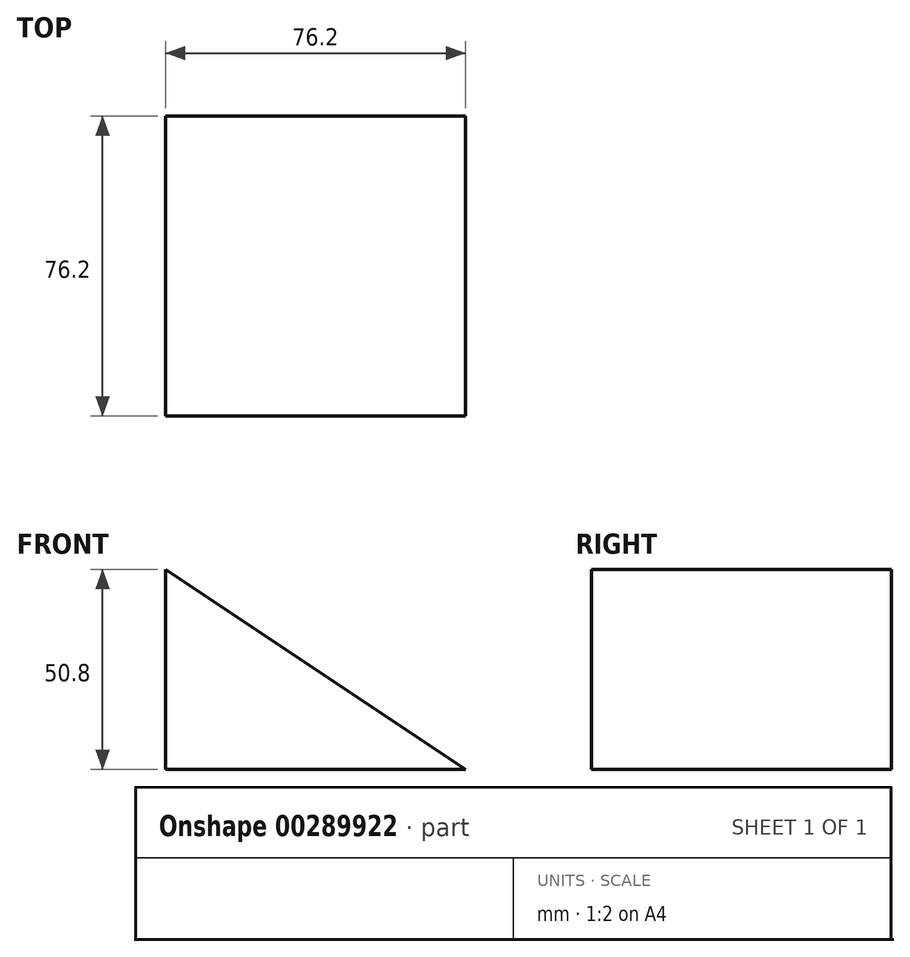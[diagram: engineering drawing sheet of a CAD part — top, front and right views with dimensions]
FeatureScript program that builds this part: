
annotation { "Feature Type Name" : "Feature", "Feature Type Description" : "" }
export const myFeature = defineFeature(function(context is Context, id is Id, definition is map)
    precondition{}
    {
        {
            var Q0;
            Q0=qCreatedBy(makeId("Front.planeOp"),FACE);
            var sketch = newSketch(context, id + "F0", { "sketchPlane" : qUnion([Q0])});
            skLineSegment(sketch, "E0", {"start": v(0, 0) * mm, "end": v(-76.2, 0) * mm});
            skLineSegment(sketch, "E1", {"start": v(-76.2, 0) * mm, "end": v(-76.2, 50.8) * mm});
            skLineSegment(sketch, "E2", {"start": v(-76.2, 50.8) * mm, "end": v(0, 0) * mm});
            skSolve(sketch);
        }
        {
            var Q0;
            Q0=makeQuery(id+"F0.imprint","IMPRINT",FACE,{"disambiguationData":[TD([[makeQuery(id+"F0.imprint","IMPRINT",EDGE,{"derivedFrom":sQuery(id+"F0.wireOp",EDGE,"E0")}),-1.0]])]});
            extrude(context, id + "F1", {"entities" : qUnion([Q0]), "depth" : 76.2 * mm});
        }
    });
